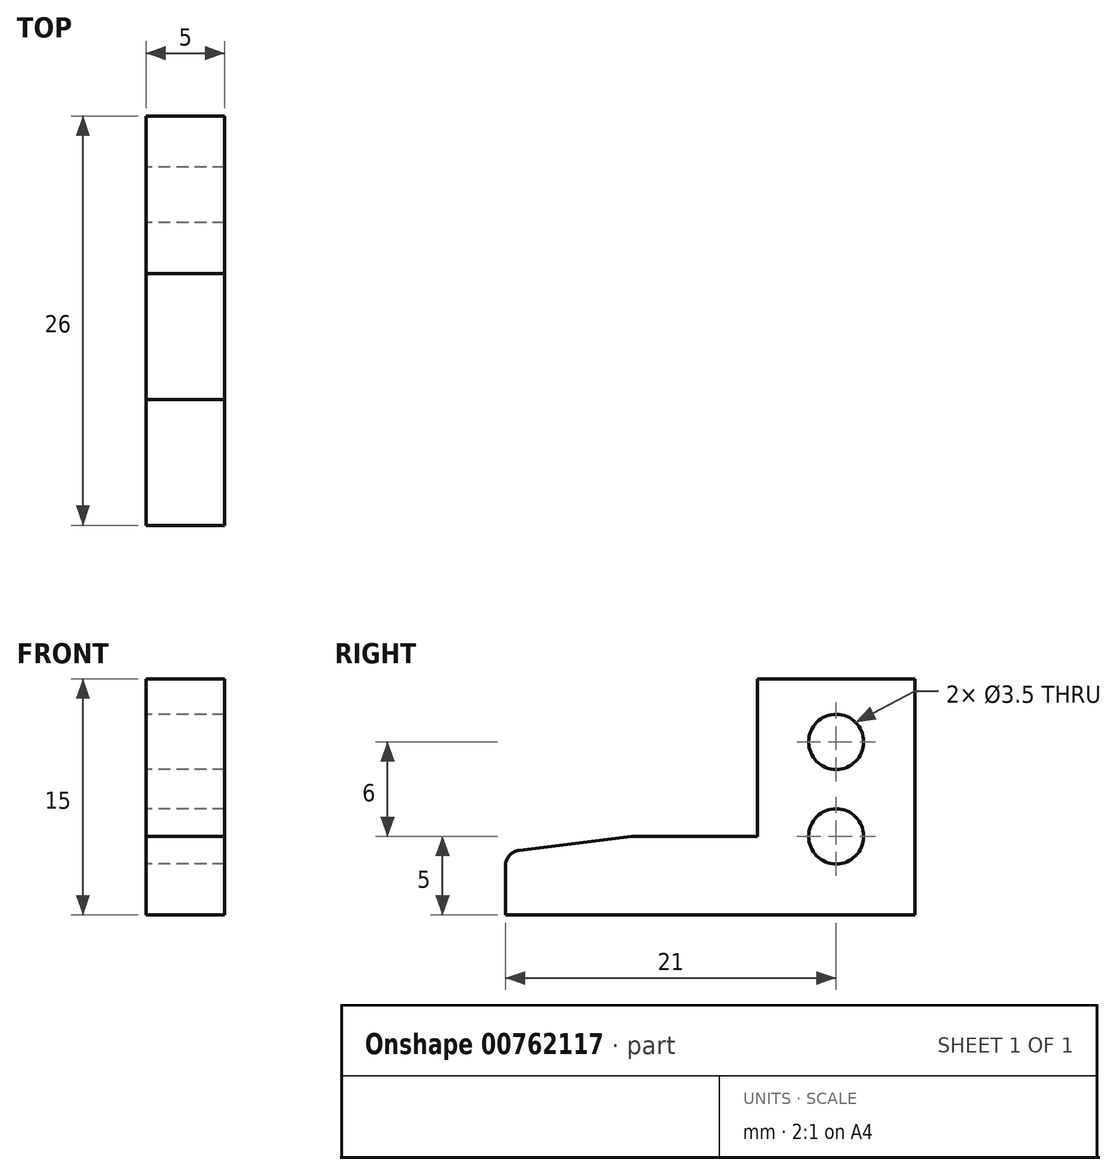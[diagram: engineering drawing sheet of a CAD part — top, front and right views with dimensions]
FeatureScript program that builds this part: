
annotation { "Feature Type Name" : "Feature", "Feature Type Description" : "" }
export const myFeature = defineFeature(function(context is Context, id is Id, definition is map)
    precondition{}
    {
        {
            var Q0;
            Q0=qCreatedBy(makeId("Right.planeOp"),FACE);
            var sketch = newSketch(context, id + "F0", { "sketchPlane" : qUnion([Q0])});
            skLineSegment(sketch, "E0", {"start": v(0, 0) * mm, "end": v(26, 0) * mm});
            skLineSegment(sketch, "E1", {"start": v(26, 0) * mm, "end": v(26, 15) * mm});
            skLineSegment(sketch, "E2", {"start": v(26, 15) * mm, "end": v(16, 15) * mm});
            skLineSegment(sketch, "E3", {"start": v(16, 15) * mm, "end": v(16, 5) * mm});
            skLineSegment(sketch, "E4", {"start": v(16, 5) * mm, "end": v(0, 5) * mm});
            skLineSegment(sketch, "E5", {"start": v(0, 5) * mm, "end": v(0, 0) * mm});
            skCircle(sketch, "E6", {"center": v(21, 5) * mm, "radius": 1.75 * mm});
            skCircle(sketch, "E7", {"center": v(21, 11) * mm, "radius": 1.75 * mm});
            skPoint(sketch, "E8", {"position": v(21, 15) * mm});
            skSolve(sketch);
        }
        {
            var Q0;
            Q0=makeQuery(id+"F0.imprint","IMPRINT",FACE,{"disambiguationData":[TD([[makeQuery(id+"F0.imprint","IMPRINT",EDGE,{"derivedFrom":sQuery(id+"F0.wireOp",EDGE,"E0")}),1.0]])]});
            extrude(context, id + "F1", {"entities" : qUnion([Q0]), "depth" : 5 * mm, "offsetDistance" : 25 * mm});
        }
        {
            var Q0;
            Q0=makeQuery(id+"F1.opExtrude","SWEPT_EDGE",EDGE,{"disambiguationData":[OSD([sQuery(id+"F0.wireOp",EDGE,"E4"),sQuery(id+"F0.wireOp",EDGE,"E5")])]});
            chamfer(context, id + "F2", {"entities" : qUnion([Q0]), "chamferType" : ChamferType.TWO_OFFSETS, "width1" : 1 * mm, "oppositeDirection" : false, "width2" : 8 * mm, "tangentPropagation" : true});
        }
        {
            var Q0;
            {var subQ0=sQuery(id+"F0.wireOp",EDGE,"E5");Q0=makeQuery(id+"F2.opChamfer","BLEND_EDGE",EDGE,{"blendedFrom":[makeQuery(id+"F1.opExtrude","SWEPT_EDGE",EDGE,{"disambiguationData":[OSD([sQuery(id+"F0.wireOp",EDGE,"E4"),subQ0])]}),makeQuery(id+"F1.opExtrude","SWEPT_FACE",FACE,{"disambiguationData":[OSD([subQ0])]})],"blendedInto":[makeQuery(id+"F1.opExtrude","SWEPT_FACE",FACE,{"disambiguationData":[OSD([subQ0])]})]});}
            fillet(context, id + "F3", {"entities" : qUnion([Q0]), "tangentPropagation" : true, "radius" : 1 * mm, "defaultsChanged" : true, "vertexSettings" : [], "allowEdgeOverflow" : false});
        }
    });
